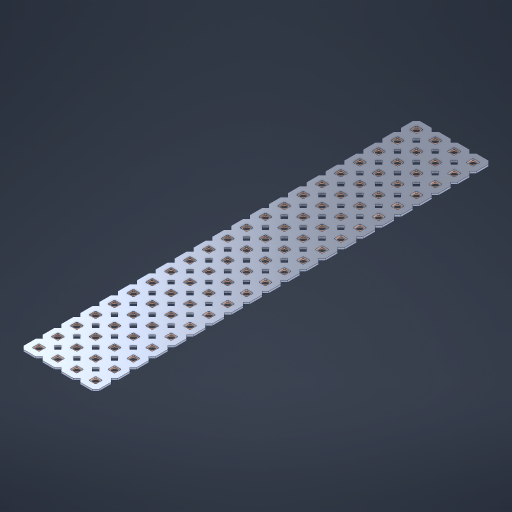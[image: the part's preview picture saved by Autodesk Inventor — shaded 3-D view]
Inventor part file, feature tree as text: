
AUTODESK INVENTOR PART (.ipt)
format: ipt  version: 2023 (Build 270158000, 158)  size: 1,231,872 bytes
history: native  units: in
note: dims shown in document units (in); Inventor stores cm internally (conversion verified against a paired STEP export)
features: other x85, extrude x83, sketch x2, pattern_linear x1
ambient origin geometry x8: Origin, YZ Plane, XZ Plane, XY Plane, X Axis, Y Axis, Z Axis, Center Point
bodies: Solid1 (feature_tree), Body (feature_tree)
feature tree (171):
  pattern_linear  "Rectangular Pattern1"  Spacing1=0.09in  [1 undecoded]
  sketch  "Sketch1"  dims[d1=0.5in]
  sketch  "Sketch2"  dims[d2=0.182in d3=0.09in d4=0.09in d5=0.09in d6=0.09in d7=0.09in d8=0.09in d9=0.09in d10=0.09in d11=0.02in d13=0.0in d14=0.172in d15=0.0625in d16=0.0in d19=0.5in d22=0.5in]
  other  "Srf1"
  other  "Srf126"
  other  "Srf127"
  other  "Srf128"
  other  "Srf129"
  other  "Srf130"
  other  "Srf131"
  other  "Srf250"
  other  "Srf251"
  other  "Srf252"
  other  "Srf253"
  other  "Srf254"
  other  "Srf255"
  other  "Srf256"
  other  "Srf257"
  other  "Srf258"
  other  "Srf259"
  other  "Srf260"
  other  "Srf261"
  other  "Srf262"
  other  "Srf263"
  other  "Srf268"
  other  "Srf269"
  other  "Srf270"
  other  "Srf271"
  other  "Srf272"
  other  "Srf273"
  other  "Srf274"
  other  "Srf275"
  other  "Srf276"
  other  "Srf277"
  other  "Srf278"
  other  "Srf279"
  other  "Srf280"
  other  "Srf281"
  other  "Srf282"
  other  "Srf283"
  other  "Srf284"
  other  "Srf285"
  other  "Srf286"
  other  "Srf287"
  other  "Srf288"
  other  "Srf293"
  other  "Srf294"
  other  "Srf295"
  other  "Srf296"
  other  "Srf297"
  other  "Srf298"
  other  "Srf299"
  other  "Srf300"
  other  "Srf301"
  other  "Srf302"
  other  "Srf303"
  other  "Srf304"
  other  "Srf305"
  other  "Srf306"
  other  "Srf307"
  other  "Srf308"
  other  "Srf309"
  other  "Srf310"
  other  "Srf311"
  other  "Srf312"
  other  "Srf313"
  other  "Srf318"
  other  "Srf319"
  other  "Srf320"
  other  "Srf321"
  other  "Srf322"
  other  "Srf323"
  other  "Srf324"
  other  "Srf325"
  other  "Srf326"
  other  "Srf327"
  other  "Srf328"
  other  "Srf329"
  other  "Srf330"
  other  "Srf331"
  other  "Srf332"
  other  "Srf333"
  other  "Srf334"
  other  "Srf335"
  other  "Srf336"
  other  "Srf337"
  other  "Srf338"
  other  "Circle"
  extrude  "ExtrusionSrf126"  Depth=0.09in
  extrude  "ExtrusionSrf127"  Depth=0.09in
  extrude  "ExtrusionSrf128"  Depth=0.09in
  extrude  "ExtrusionSrf129"  Depth=0.09in
  extrude  "ExtrusionSrf130"  Depth=0.09in
  extrude  "ExtrusionSrf131"  Depth=0.09in
  extrude  "ExtrusionSrf250"  Depth=0.09in
  extrude  "ExtrusionSrf251"  Depth=0.02in
  extrude  "ExtrusionSrf252"  TaperAngle=0.0deg  [1 undecoded]
  extrude  "ExtrusionSrf253"  Depth=0.5in
  extrude  "ExtrusionSrf254"  Depth=0.5in TaperAngle=0.0deg
  extrude  "ExtrusionSrf255"  Depth=0.5in
  extrude  "ExtrusionSrf256"  Depth=0.5in
  extrude  "ExtrusionSrf257"  [1 undecoded]
  extrude  "ExtrusionSrf258"  [1 undecoded]
  extrude  "ExtrusionSrf259"  [1 undecoded]
  extrude  "ExtrusionSrf260"  [1 undecoded]
  extrude  "ExtrusionSrf261"  [1 undecoded]
  extrude  "ExtrusionSrf262"  [1 undecoded]
  extrude  "ExtrusionSrf263"  [1 undecoded]
  extrude  "ExtrusionSrf268"  [1 undecoded]
  extrude  "ExtrusionSrf269"  [1 undecoded]
  extrude  "ExtrusionSrf270"  [1 undecoded]
  extrude  "ExtrusionSrf271"  [1 undecoded]
  extrude  "ExtrusionSrf272"  [1 undecoded]
  extrude  "ExtrusionSrf273"  [1 undecoded]
  extrude  "ExtrusionSrf274"  [1 undecoded]
  extrude  "ExtrusionSrf275"  [1 undecoded]
  extrude  "ExtrusionSrf276"  [1 undecoded]
  extrude  "ExtrusionSrf277"  [1 undecoded]
  extrude  "ExtrusionSrf278"  [1 undecoded]
  extrude  "ExtrusionSrf279"  [1 undecoded]
  extrude  "ExtrusionSrf280"  [1 undecoded]
  extrude  "ExtrusionSrf281"  [1 undecoded]
  extrude  "ExtrusionSrf282"  [1 undecoded]
  extrude  "ExtrusionSrf283"  [1 undecoded]
  extrude  "ExtrusionSrf284"  [1 undecoded]
  extrude  "ExtrusionSrf285"  [1 undecoded]
  extrude  "ExtrusionSrf286"  [1 undecoded]
  extrude  "ExtrusionSrf287"  [1 undecoded]
  extrude  "ExtrusionSrf288"  [1 undecoded]
  extrude  "ExtrusionSrf293"  [1 undecoded]
  extrude  "ExtrusionSrf294"  [1 undecoded]
  extrude  "ExtrusionSrf295"  [1 undecoded]
  extrude  "ExtrusionSrf296"  [1 undecoded]
  extrude  "ExtrusionSrf297"  [1 undecoded]
  extrude  "ExtrusionSrf298"  [1 undecoded]
  extrude  "ExtrusionSrf299"  [1 undecoded]
  extrude  "ExtrusionSrf300"  [1 undecoded]
  extrude  "ExtrusionSrf301"  [1 undecoded]
  extrude  "ExtrusionSrf302"  [1 undecoded]
  extrude  "ExtrusionSrf303"  [1 undecoded]
  extrude  "ExtrusionSrf304"  [1 undecoded]
  extrude  "ExtrusionSrf305"  [1 undecoded]
  extrude  "ExtrusionSrf306"  [1 undecoded]
  extrude  "ExtrusionSrf307"  [1 undecoded]
  extrude  "ExtrusionSrf308"  [1 undecoded]
  extrude  "ExtrusionSrf309"  [1 undecoded]
  extrude  "ExtrusionSrf310"  [1 undecoded]
  extrude  "ExtrusionSrf311"  [1 undecoded]
  extrude  "ExtrusionSrf312"  [1 undecoded]
  extrude  "ExtrusionSrf313"  [1 undecoded]
  extrude  "ExtrusionSrf318"  [1 undecoded]
  extrude  "ExtrusionSrf319"  [1 undecoded]
  extrude  "ExtrusionSrf320"  [1 undecoded]
  extrude  "ExtrusionSrf321"  [1 undecoded]
  extrude  "ExtrusionSrf322"  [1 undecoded]
  extrude  "ExtrusionSrf323"  [1 undecoded]
  extrude  "ExtrusionSrf324"  [1 undecoded]
  extrude  "ExtrusionSrf325"  [1 undecoded]
  extrude  "ExtrusionSrf326"  [1 undecoded]
  extrude  "ExtrusionSrf327"  [1 undecoded]
  extrude  "ExtrusionSrf328"  [1 undecoded]
  extrude  "ExtrusionSrf329"  [1 undecoded]
  extrude  "ExtrusionSrf330"  [1 undecoded]
  extrude  "ExtrusionSrf331"  [1 undecoded]
  extrude  "ExtrusionSrf332"  [1 undecoded]
  extrude  "ExtrusionSrf333"  [1 undecoded]
  extrude  "ExtrusionSrf334"  [1 undecoded]
  extrude  "ExtrusionSrf335"  [1 undecoded]
  extrude  "ExtrusionSrf336"  [1 undecoded]
  extrude  "ExtrusionSrf337"  [1 undecoded]
  extrude  "ExtrusionSrf338"  [1 undecoded]
note: 72 required parameter values undecoded (feature->parameter linkage not recoverable at this tier; creation-order binding heuristic only, values carry confidence <= 0.55)
